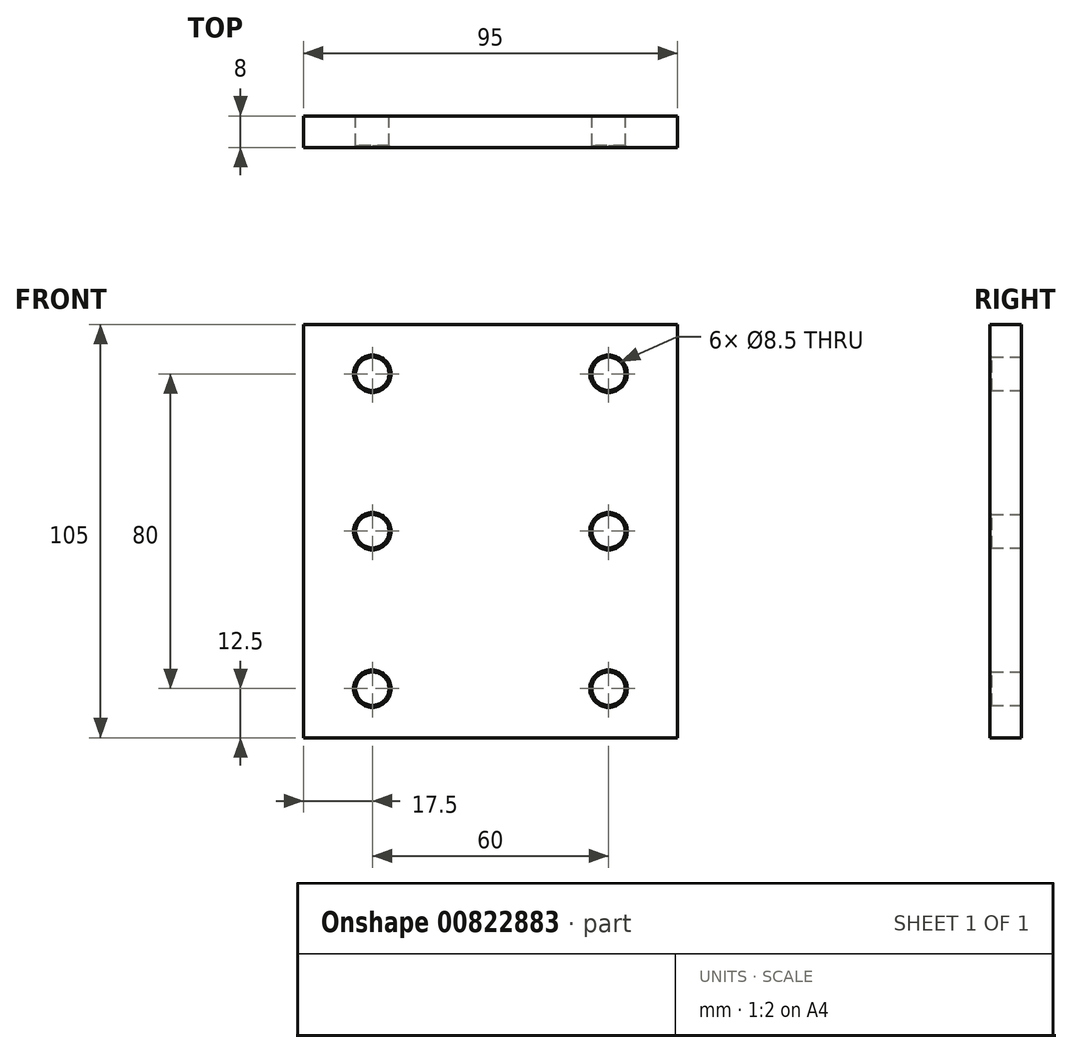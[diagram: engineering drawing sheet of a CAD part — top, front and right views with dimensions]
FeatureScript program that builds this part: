
annotation { "Feature Type Name" : "Feature", "Feature Type Description" : "" }
export const myFeature = defineFeature(function(context is Context, id is Id, definition is map)
    precondition{}
    {
        {
            var Q0;
            Q0=qCreatedBy(makeId("Front.planeOp"),FACE);
            var sketch = newSketch(context, id + "F0", { "sketchPlane" : qUnion([Q0])});
            skLineSegment(sketch, "E0.bottom", {"start": v(50, -52.5) * mm, "end": v(-45, -52.5) * mm});
            skLineSegment(sketch, "E0.top", {"start": v(50, 52.5) * mm, "end": v(-45, 52.5) * mm});
            skLineSegment(sketch, "E0.left", {"start": v(50, -52.5) * mm, "end": v(50, 52.5) * mm});
            skLineSegment(sketch, "E0.right", {"start": v(-45, -52.5) * mm, "end": v(-45, 52.5) * mm});
            skLineSegment(sketch, "E1", {"start": v(2.5, 0) * mm, "end": v(0, 0) * mm, "construction": true});
            skLineSegment(sketch, "E2.bottom", {"start": v(-27.5, 40) * mm, "end": v(32.5, 40) * mm, "construction": true});
            skLineSegment(sketch, "E2.top", {"start": v(-27.5, -40) * mm, "end": v(32.5, -40) * mm, "construction": true});
            skLineSegment(sketch, "E2.left", {"start": v(-27.5, 40) * mm, "end": v(-27.5, -40) * mm, "construction": true});
            skLineSegment(sketch, "E2.right", {"start": v(32.5, 40) * mm, "end": v(32.5, -40) * mm, "construction": true});
            skPoint(sketch, "E2.middle", {"position": v(2.5, 0) * mm});
            skCircle(sketch, "E3", {"center": v(-27.5, 40) * mm, "radius": 4.25 * mm});
            skCircle(sketch, "E4", {"center": v(32.5, 40) * mm, "radius": 4.25 * mm});
            skCircle(sketch, "E5", {"center": v(32.5, -40) * mm, "radius": 4.25 * mm});
            skCircle(sketch, "E6", {"center": v(-27.5, -40) * mm, "radius": 4.25 * mm});
            skCircle(sketch, "E7", {"center": v(-27.5, -40) * mm, "radius": 9 * mm, "construction": true});
            skLineSegment(sketch, "E8", {"start": v(-27.5, 0) * mm, "end": v(32.5, 0) * mm, "construction": true});
            skCircle(sketch, "E9", {"center": v(-27.5, 0) * mm, "radius": 4.25 * mm});
            skCircle(sketch, "E10", {"center": v(32.5, 0) * mm, "radius": 4.25 * mm});
            skSolve(sketch);
        }
        {
            var Q0;
            Q0 = qSketchRegion(id + "F0", true);
            extrude(context, id + "F1", {"entities" : qUnion([Q0]), "depth" : 8 * mm, "offsetDistance" : 25 * mm});
        }
        {
            var Q0;
            Q0=makeQuery(id+"F1.opExtrude","CAP_EDGE",EDGE,{"disambiguationData":[OSD([sQuery(id+"F0.wireOp",EDGE,"E3")])],"isStart":false});
            var Q1;
            Q1=makeQuery(id+"F1.opExtrude","CAP_EDGE",EDGE,{"disambiguationData":[OSD([sQuery(id+"F0.wireOp",EDGE,"E4")])],"isStart":false});
            var Q2;
            Q2=makeQuery(id+"F1.opExtrude","CAP_EDGE",EDGE,{"disambiguationData":[OSD([sQuery(id+"F0.wireOp",EDGE,"E5")])],"isStart":false});
            var Q3;
            Q3=makeQuery(id+"F1.opExtrude","CAP_EDGE",EDGE,{"disambiguationData":[OSD([sQuery(id+"F0.wireOp",EDGE,"E6")])],"isStart":false});
            var Q4;
            Q4=makeQuery(id+"F1.opExtrude","CAP_EDGE",EDGE,{"disambiguationData":[OSD([sQuery(id+"F0.wireOp",EDGE,"E9")])],"isStart":false});
            var Q5;
            Q5=makeQuery(id+"F1.opExtrude","CAP_EDGE",EDGE,{"disambiguationData":[OSD([sQuery(id+"F0.wireOp",EDGE,"E10")])],"isStart":false});
            chamfer(context, id + "F2", {"entities" : qUnion([Q0, Q1, Q2, Q3, Q4, Q5]), "width" : 0.5 * mm, "tangentPropagation" : true});
        }
    });
